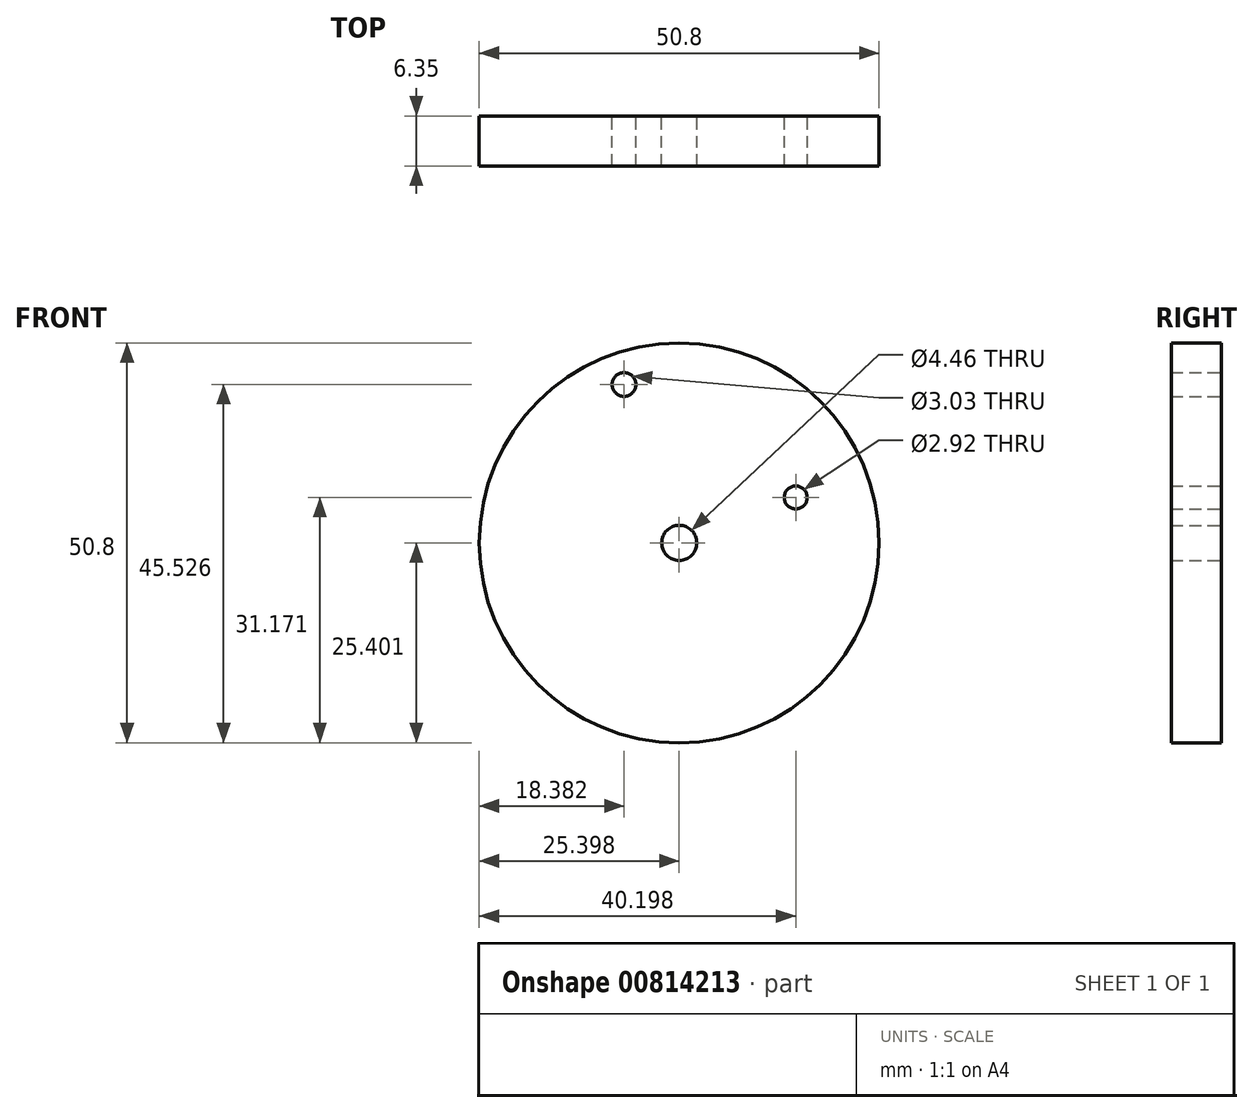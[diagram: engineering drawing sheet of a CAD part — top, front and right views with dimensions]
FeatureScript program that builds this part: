
annotation { "Feature Type Name" : "Feature", "Feature Type Description" : "" }
export const myFeature = defineFeature(function(context is Context, id is Id, definition is map)
    precondition{}
    {
        {
            var Q0;
            Q0=qCreatedBy(makeId("Front.planeOp"),FACE);
            var sketch = newSketch(context, id + "F0", { "sketchPlane" : qUnion([Q0])});
            skCircle(sketch, "E0", {"center": v(-37.05, 34.2) * mm, "radius": 25.4 * mm});
            skCircle(sketch, "E1", {"center": v(-37.05, 34.2) * mm, "radius": 2.23 * mm});
            skCircle(sketch, "E2", {"center": v(-44.07, 54.33) * mm, "radius": 1.51 * mm});
            skCircle(sketch, "E3", {"center": v(-22.25, 39.97) * mm, "radius": 1.46 * mm});
            skSolve(sketch);
        }
        {
            var Q0;
            Q0=makeQuery(id+"F0.imprint","IMPRINT",FACE,{"disambiguationData":[TD([[makeQuery(id+"F0.imprint","IMPRINT",EDGE,{"derivedFrom":sQuery(id+"F0.wireOp",EDGE,"E0")}),1.0]])]});
            extrude(context, id + "F1", {"entities" : qUnion([Q0]), "depth" : 6.35 * mm, "offsetDistance" : 25.4 * mm});
        }
    });
